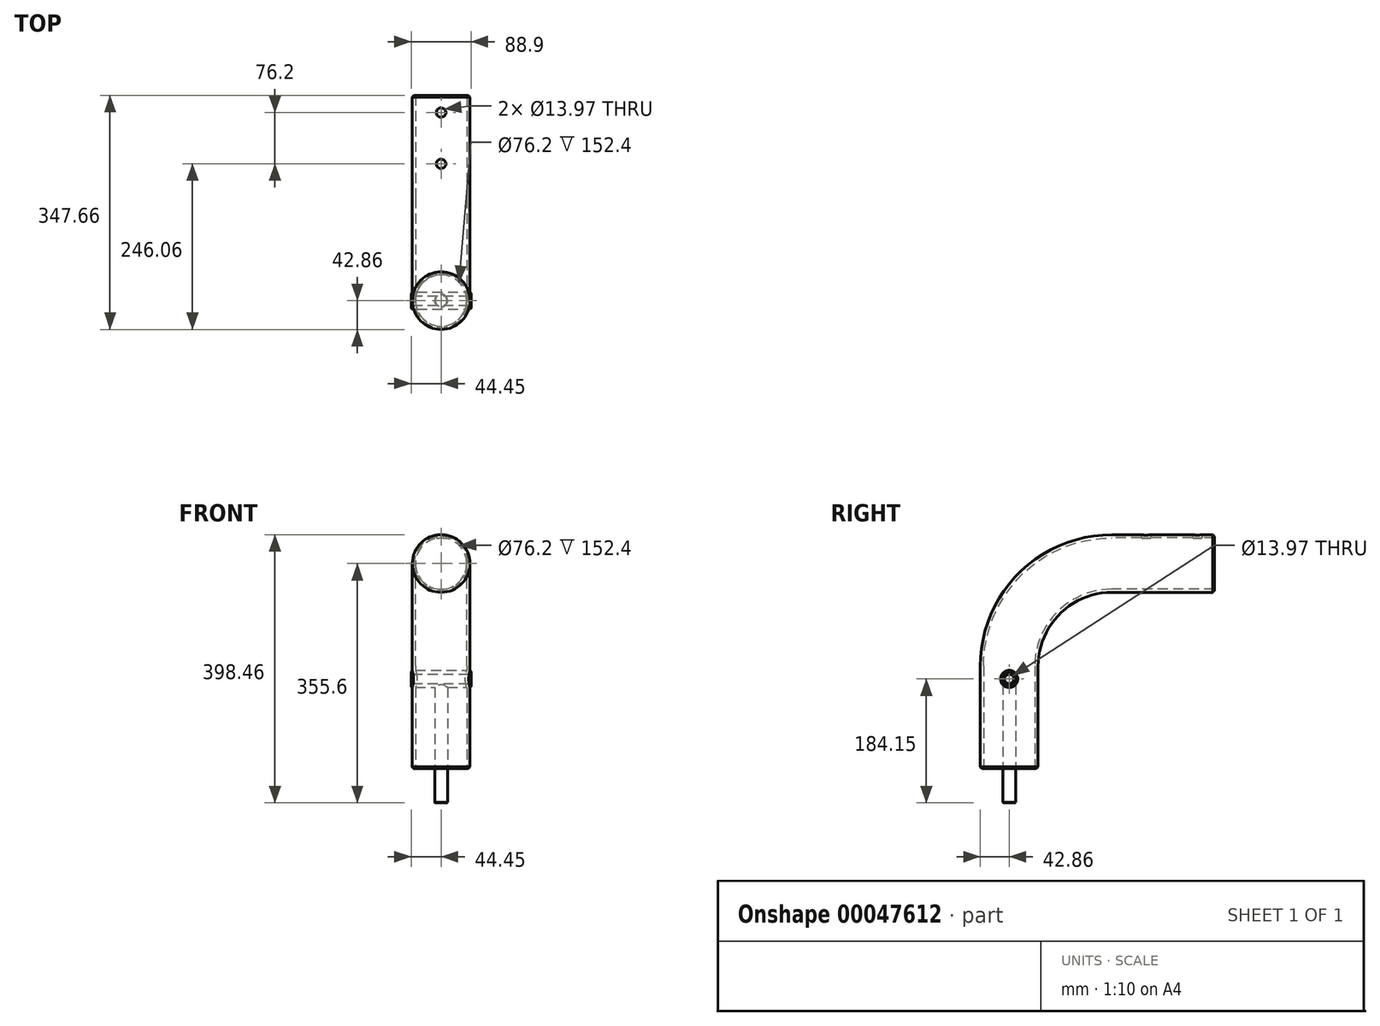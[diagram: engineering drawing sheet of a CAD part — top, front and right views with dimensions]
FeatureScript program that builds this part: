
annotation { "Feature Type Name" : "Feature", "Feature Type Description" : "" }
export const myFeature = defineFeature(function(context is Context, id is Id, definition is map)
    precondition{}
    {
        {
            var Q0;
            Q0=qCreatedBy(makeId("Front.planeOp"),FACE);
            var sketch = newSketch(context, id + "F0", { "sketchPlane" : qUnion([Q0])});
            skCircle(sketch, "E0", {"center": v(0, 0) * mm, "radius": 42.86 * mm});
            skCircle(sketch, "E1", {"center": v(0, 0) * mm, "radius": 38.1 * mm});
            skSolve(sketch);
        }
        {
            var Q0;
            Q0=qCreatedBy(makeId("Right.planeOp"),FACE);
            var sketch = newSketch(context, id + "F1", { "sketchPlane" : qUnion([Q0])});
            skLineSegment(sketch, "E2", {"start": v(0, 0) * mm, "end": v(-152.4, 0) * mm});
            skLineSegment(sketch, "E3", {"start": v(-304.8, -152.4) * mm, "end": v(-304.8, -304.8) * mm});
            skPoint(sketch, "E4.visualSharp", {"position": v(-304.8, 0) * mm});
            skArc(sketch, "E4.filletArc", {"start": v(-152.4, 0) * mm, "mid": v(-260.16, -44.64) * mm, "end": v(-304.8, -152.4) * mm});
            skSolve(sketch);
        }
        {
            var Q0;
            Q0=qSketchRegion(id+"F0",true);
            var Q1;
            Q1=qConstructionFilter(qBodyType(qCreatedBy(id+"F1",EDGE),BodyType.WIRE),ConstructionObject.NO);
            sweep(context, id + "F2", {"profiles" : qUnion([Q0]), "path" : qUnion([Q1])});
        }
        {
            var Q0;
            Q0=qCreatedBy(makeId("Top.planeOp"),FACE);
            var sketch = newSketch(context, id + "F3", { "sketchPlane" : qUnion([Q0])});
            skCircle(sketch, "E5", {"center": v(0, -25.4) * mm, "radius": 6.99 * mm});
            skCircle(sketch, "E6", {"center": v(0, -101.6) * mm, "radius": 6.99 * mm});
            skLineSegment(sketch, "E7", {"start": v(0, 0) * mm, "end": v(0, -119.2) * mm, "construction": true});
            skSolve(sketch);
        }
        {
            var Q0;
            Q0=qSketchRegion(id+"F3",true);
            var Q1;
            Q1=makeQuery(id+"F2.opSweep","SWEPT_FACE",FACE,{"disambiguationData":[OSD([sQuery(id+"F0.wireOp",EDGE,"E0"),sQuery(id+"F1.wireOp",EDGE,"E2")])]});
            var Q2;
            Q2=makeQuery(id+"F2.opSweep","SWEPT_BODY",BODY,{"disambiguationData":[OSD([sQuery(id+"F0.wireOp",EDGE,"E0"),sQuery(id+"F0.wireOp",EDGE,"E1"),sQuery(id+"F1.wireOp",EDGE,"E3")])]});
            extrude(context, id + "F4", {"entities" : qUnion([Q0]), "operationType" : NewBodyOperationType.REMOVE, "endBound" : BoundingType.UP_TO_SURFACE, "endBoundEntityFace" : qUnion([Q1]), "endBoundEntityBody" : qUnion([Q2]), "depth" : 25.4 * mm});
        }
        {
            var Q0;
            Q0=qCreatedBy(makeId("Right.planeOp"),FACE);
            cPlane(context, id + "F5", {"entities" : qUnion([Q0]), "cplaneType" : CPlaneType.OFFSET, "offset" : 44.45 * mm, "width" : 152.4 * mm, "height" : 152.4 * mm});
        }
        {
            var Q0;
            Q0=qCreatedBy(id+"F5.planeOp",FACE);
            var sketch = newSketch(context, id + "F6", { "sketchPlane" : qUnion([Q0])});
            skCircle(sketch, "E8", {"center": v(-304.8, -171.45) * mm, "radius": 12.7 * mm});
            skCircle(sketch, "E9", {"center": v(-304.8, -171.45) * mm, "radius": 6.99 * mm});
            skSolve(sketch);
        }
        {
            var Q0;
            Q0=qSketchRegion(id+"F6",true);
            extrude(context, id + "F7", {"entities" : qUnion([Q0]), "operationType" : NewBodyOperationType.ADD, "oppositeDirection" : true, "depth" : 88.9 * mm});
        }
        {
            var Q0;
            Q0=makeQuery(id+"F7.opExtrude","CAP_FACE",FACE,{"disambiguationData":[OSD([sQuery(id+"F6.wireOp",EDGE,"E8"),sQuery(id+"F6.wireOp",EDGE,"E9")])],"isStart":true});
            var sketch = newSketch(context, id + "F8", { "sketchPlane" : qUnion([Q0])});
            skCircle(sketch, "E10", {"center": v(-304.8, -171.45) * mm, "radius": 6.99 * mm});
            skSolve(sketch);
        }
        {
            var Q0;
            Q0=qSketchRegion(id+"F8",true);
            extrude(context, id + "F9", {"entities" : qUnion([Q0]), "operationType" : NewBodyOperationType.REMOVE, "oppositeDirection" : true, "depth" : 88.9 * mm});
        }
        {
            var Q0;
            Q0=makeQuery(id+"F4.boolean.opBoolean","COPY",EDGE,{"derivedFrom":makeQuery(id+"F4.opExtrude","CAP_EDGE",EDGE,{"disambiguationData":[OSD([sQuery(id+"F3.wireOp",EDGE,"E6")])],"isStart":false})});
            var Q1;
            Q1=makeQuery(id+"F4.boolean.opBoolean","COPY",EDGE,{"derivedFrom":makeQuery(id+"F4.opExtrude","CAP_EDGE",EDGE,{"disambiguationData":[OSD([sQuery(id+"F3.wireOp",EDGE,"E5")])],"isStart":false})});
            var Q2;
            Q2=makeQuery(id+"F7.opExtrude","CAP_EDGE",EDGE,{"disambiguationData":[OSD([sQuery(id+"F6.wireOp",EDGE,"E9")])],"isStart":true});
            var Q3;
            Q3=makeQuery(id+"F7.opExtrude","CAP_EDGE",EDGE,{"disambiguationData":[OSD([sQuery(id+"F6.wireOp",EDGE,"E8")])],"isStart":true});
            var Q4;
            Q4=makeQuery(id+"F7.opExtrude","CAP_EDGE",EDGE,{"disambiguationData":[OSD([sQuery(id+"F6.wireOp",EDGE,"E8")])],"isStart":false});
            var Q5;
            Q5=makeQuery(id+"F7.opExtrude","CAP_EDGE",EDGE,{"disambiguationData":[OSD([sQuery(id+"F6.wireOp",EDGE,"E9")])],"isStart":false});
            chamfer(context, id + "F10", {"entities" : qUnion([Q0, Q1, Q2, Q3, Q4, Q5]), "width" : 1.59 * mm, "tangentPropagation" : true});
        }
        {
            var Q0;
            Q0=makeQuery(id+"F2.opSweep","CAP_EDGE",EDGE,{"disambiguationData":[OSD([sQuery(id+"F0.wireOp",EDGE,"E0"),sQuery(id+"F1.wireOp",VERTEX,"E2.start")])],"isStart":true});
            var Q1;
            Q1=makeQuery(id+"F2.opSweep","CAP_EDGE",EDGE,{"disambiguationData":[OSD([sQuery(id+"F0.wireOp",EDGE,"E0"),sQuery(id+"F1.wireOp",VERTEX,"E3.end")])],"isStart":false});
            chamfer(context, id + "F11", {"entities" : qUnion([Q0, Q1]), "width" : 2.54 * mm, "tangentPropagation" : true});
        }
        {
            var Q0;
            Q0=makeQuery(id+"F2.opSweep","CAP_FACE",FACE,{"disambiguationData":[OSD([sQuery(id+"F0.wireOp",EDGE,"E0"),sQuery(id+"F0.wireOp",EDGE,"E1"),sQuery(id+"F1.wireOp",VERTEX,"E3.end")])],"isStart":false});
            cPlane(context, id + "F12", {"entities" : qUnion([Q0]), "cplaneType" : CPlaneType.OFFSET, "offset" : 50.8 * mm, "width" : 152.4 * mm, "height" : 152.4 * mm});
        }
        {
            var Q0;
            Q0=qCreatedBy(id+"F12.planeOp",FACE);
            var sketch = newSketch(context, id + "F13", { "sketchPlane" : qUnion([Q0])});
            skCircle(sketch, "E11", {"center": v(0, 304.8) * mm, "radius": 9.53 * mm});
            skSolve(sketch);
        }
        {
            var Q0;
            Q0=qSketchRegion(id+"F13",true);
            var Q1;
            Q1=makeQuery(id+"F7.boolean.opBoolean","SPLIT",FACE,{"disambiguationData":[TD([makeQuery(id+"F2.opSweep","SWEPT_FACE",FACE,{"disambiguationData":[OSD([sQuery(id+"F0.wireOp",EDGE,"E1"),sQuery(id+"F1.wireOp",EDGE,"E3")])]})])],"derivedFrom":makeQuery(id+"F7.opExtrude","SWEPT_FACE",FACE,{"disambiguationData":[OSD([sQuery(id+"F6.wireOp",EDGE,"E8")])]})});
            extrude(context, id + "F14", {"entities" : qUnion([Q0]), "operationType" : NewBodyOperationType.ADD, "endBound" : BoundingType.UP_TO_SURFACE, "oppositeDirection" : true, "endBoundEntityFace" : qUnion([Q1]), "depth" : 25.4 * mm});
        }
        {
            var Q0;
            Q0=makeQuery(id+"F14.opExtrude","CAP_EDGE",EDGE,{"disambiguationData":[OSD([sQuery(id+"F13.wireOp",EDGE,"E11")])],"isStart":true});
            chamfer(context, id + "F15", {"entities" : qUnion([Q0]), "width" : 0.8 * mm, "tangentPropagation" : true});
        }
    });
